# Revit family: Granit_2_ość-Projekt_Granit
name_source: partatom
category: Drzwi
revit_build: Autodesk Revit 2016 (Build: 20150714_1515(x64)
units: mm (PartAtom-declared; Revit-internal decimal feet)

## family parameters
Numer OmniClass = 23.30.10.00
Obiekt nadrzędny = Ściana
Punkt obliczania pomieszczeń = Nie
Tnij formami wycięć po wczytaniu = Nie
Tytuł OmniClass = Doors
Współdzielony = Nie
Zawsze pionowo = Tak

## types (3) — shared parameters
Funkcja = Wewnętrzna
Informacja = Własność Porta KMI Poland, wszelkie prawa zastrzeżone.
Konstrukcja analityczna = <Brak>
Materiał klamka = <Wg kategorii>
Materiał ościeżnica = <Wg kategorii>
Materiał ościeżnica metalowa = <Wg kategorii>
Materiał skrzydło = <Wg kategorii>
Model = Granit 2
Producent = PORTA KMI Poland
URL = www.porta.com.pl
Wysokość = 2016 mm
Wysokość brutto = 2070 mm  [stored 6.79134 ft]
Zakończenie ściany = Wg obiektu nadrzędnego

## per-type parameters (varying)
| type | Szerokość | Szerokość brutto | Szerokość skrzydła |
| 80 | 796 mm  [stored 2.61155 ft] | 900 mm  [stored 2.95276 ft] | 844 mm  [stored 2.76903 ft] |
| 90 | 904 mm | 1010 mm | 952 mm |
| 100 | 996 mm | 1100 mm | 1044 mm |

note: [stored X ft] marks values corroborated as IEEE doubles in the binary element streams (Revit-internal decimal feet)

## geometry (parser evidence)
native form markers: Blend x4, Sweep x1
no freeform markers — native parametric forms only
